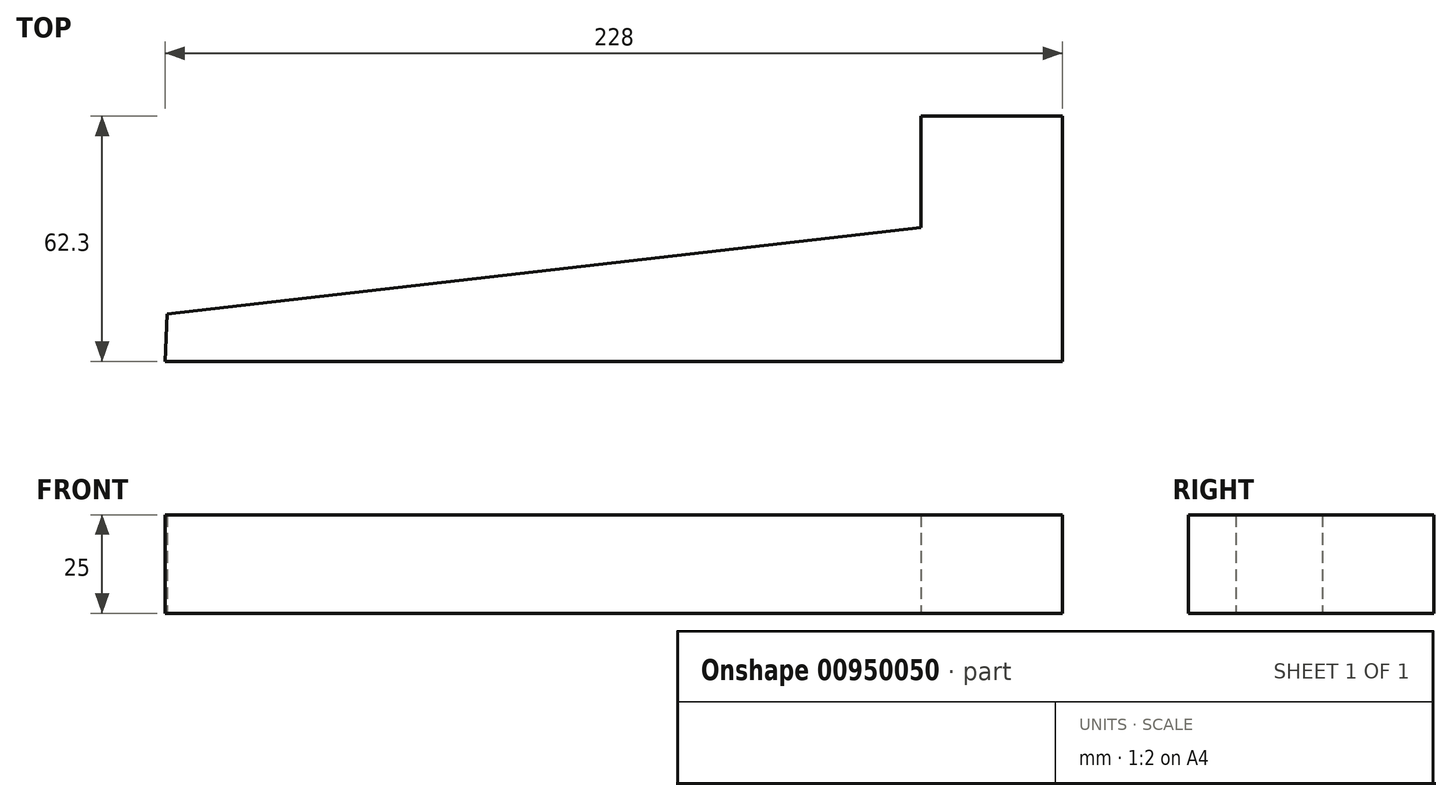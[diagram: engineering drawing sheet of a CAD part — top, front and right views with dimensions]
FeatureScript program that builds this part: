
annotation { "Feature Type Name" : "Feature", "Feature Type Description" : "" }
export const myFeature = defineFeature(function(context is Context, id is Id, definition is map)
    precondition{}
    {
        {
            var Q0;
            Q0=qCreatedBy(makeId("Top.planeOp"),FACE);
            var sketch = newSketch(context, id + "F0", { "sketchPlane" : qUnion([Q0])});
            skLineSegment(sketch, "E0", {"start": v(-37.01, 28.3) * mm, "end": v(-37.01, 0) * mm});
            skLineSegment(sketch, "E1", {"start": v(-37.01, 28.3) * mm, "end": v(-1.01, 28.3) * mm});
            skLineSegment(sketch, "E2", {"start": v(-1.01, 28.3) * mm, "end": v(-1.01, -34) * mm});
            skLineSegment(sketch, "E3", {"start": v(-1.01, -34) * mm, "end": v(-229.01, -34) * mm});
            skLineSegment(sketch, "E4", {"start": v(-37.01, 0) * mm, "end": v(-228.48, -22.01) * mm});
            skLineSegment(sketch, "E5", {"start": v(-228.48, -22.01) * mm, "end": v(-229.01, -34) * mm});
            skSolve(sketch);
        }
        {
            var Q0;
            Q0 = qSketchRegion(id + "F0", true);
            extrude(context, id + "F1", {"entities" : qUnion([Q0]), "depth" : 25 * mm, "offsetDistance" : 25 * mm});
        }
        {
            var Q0;
            Q0 = qSketchRegion(id + "F0", true);
            extrude(context, id + "F2", {"entities" : qUnion([Q0]), "operationType" : NewBodyOperationType.ADD, "depth" : 25 * mm, "offsetDistance" : 25 * mm});
        }
    });
